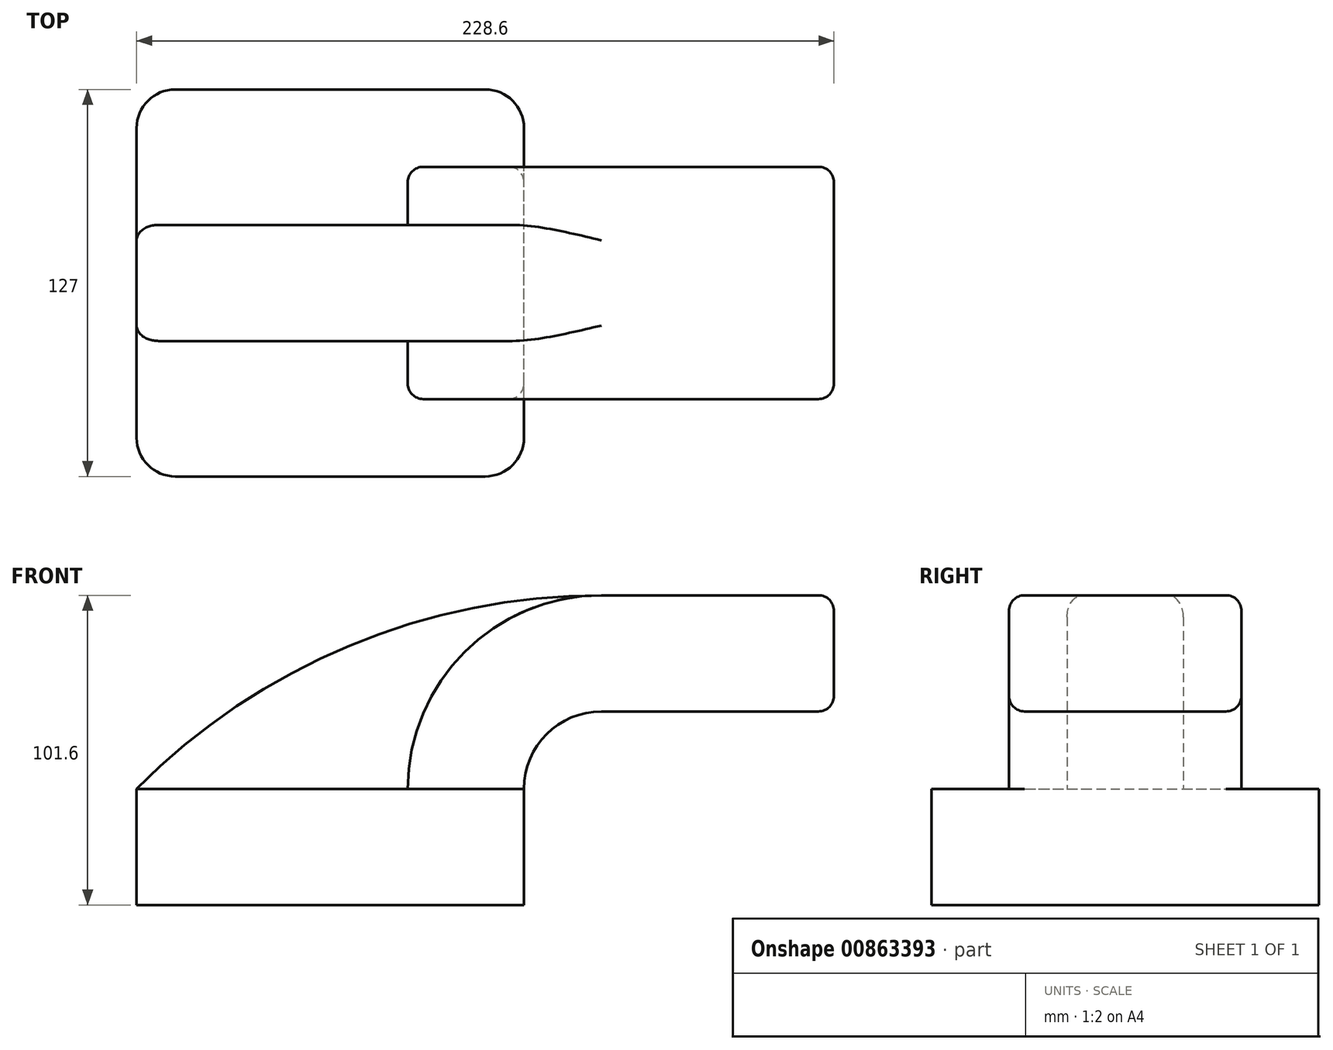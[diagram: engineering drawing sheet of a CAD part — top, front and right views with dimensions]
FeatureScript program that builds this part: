
annotation { "Feature Type Name" : "Feature", "Feature Type Description" : "" }
export const myFeature = defineFeature(function(context is Context, id is Id, definition is map)
    precondition{}
    {
        {
            var Q0;
            Q0=qCreatedBy(makeId("Front.planeOp"),FACE);
            var sketch = newSketch(context, id + "F0", { "sketchPlane" : qUnion([Q0])});
            skLineSegment(sketch, "E0.bottom", {"start": v(63.5, -19.05) * mm, "end": v(-63.5, -19.05) * mm});
            skLineSegment(sketch, "E0.top", {"start": v(63.5, 19.05) * mm, "end": v(-63.5, 19.05) * mm});
            skLineSegment(sketch, "E0.left", {"start": v(63.5, -19.05) * mm, "end": v(63.5, 19.05) * mm});
            skLineSegment(sketch, "E0.right", {"start": v(-63.5, -19.05) * mm, "end": v(-63.5, 19.05) * mm});
            skPoint(sketch, "E0.middle", {"position": v(0, 0) * mm});
            skPoint(sketch, "E1.middle", {"position": v(0, -116.97) * mm});
            skLineSegment(sketch, "E2.bottom", {"start": v(88.9, 44.45) * mm, "end": v(165.1, 44.45) * mm});
            skLineSegment(sketch, "E2.top", {"start": v(88.9, 82.55) * mm, "end": v(165.1, 82.55) * mm});
            skLineSegment(sketch, "E2.left", {"start": v(88.9, 44.45) * mm, "end": v(88.9, 82.55) * mm});
            skLineSegment(sketch, "E2.right", {"start": v(165.1, 44.45) * mm, "end": v(165.1, 82.55) * mm});
            skPoint(sketch, "E2.middle", {"position": v(127, 63.5) * mm});
            skArc(sketch, "E3", {"start": v(88.9, 44.45) * mm, "mid": v(70.94, 37.01) * mm, "end": v(63.5, 19.05) * mm});
            skArc(sketch, "E4.0", {"start": v(88.9, 82.55) * mm, "mid": v(44, 63.95) * mm, "end": v(25.4, 19.05) * mm});
            skArc(sketch, "E5", {"start": v(88.9, 82.55) * mm, "mid": v(6.35, 66.04) * mm, "end": v(-63.5, 19.05) * mm});
            skSolve(sketch);
        }
        {
            var Q0;
            Q0=makeQuery(id+"F0.imprint","IMPRINT",FACE,{"disambiguationData":[TD([[makeQuery(id+"F0.imprint","IMPRINT",EDGE,{"derivedFrom":sQuery(id+"F0.wireOp",EDGE,"E0.bottom")}),-1.0]])]});
            extrude(context, id + "F1", {"entities" : qUnion([Q0]), "endBound" : BoundingType.SYMMETRIC, "depth" : 127 * mm, "offsetDistance" : 25.4 * mm});
        }
        {
            var Q0;
            {var subQ2=sQuery(id+"F0.wireOp",EDGE,"E4.0");Q0=makeQuery(id+"F0.imprint","IMPRINT",FACE,{"disambiguationData":[TD([[makeQuery(id+"F0.imprint","IMPRINT",EDGE,{"derivedFrom":subQ2}),-1.0]])]});}
            extrude(context, id + "F2", {"entities" : qUnion([Q0]), "operationType" : NewBodyOperationType.ADD, "endBound" : BoundingType.SYMMETRIC, "depth" : 38.1 * mm, "offsetDistance" : 25.4 * mm});
        }
        {
            var Q0;
            Q0=makeQuery(id+"F0.imprint","IMPRINT",FACE,{"disambiguationData":[TD([[makeQuery(id+"F0.imprint","IMPRINT",EDGE,{"derivedFrom":sQuery(id+"F0.wireOp",EDGE,"E2.left")}),1.0]])]});
            extrude(context, id + "F3", {"entities" : qUnion([Q0]), "operationType" : NewBodyOperationType.ADD, "endBound" : BoundingType.SYMMETRIC, "depth" : 76.2 * mm, "offsetDistance" : 25.4 * mm});
        }
        {
            var Q0;
            Q0=makeQuery(id+"F0.imprint","IMPRINT",FACE,{"disambiguationData":[TD([[makeQuery(id+"F0.imprint","IMPRINT",EDGE,{"derivedFrom":sQuery(id+"F0.wireOp",EDGE,"E2.bottom")}),1.0]])]});
            extrude(context, id + "F4", {"entities" : qUnion([Q0]), "operationType" : NewBodyOperationType.ADD, "endBound" : BoundingType.SYMMETRIC, "depth" : 76.2 * mm, "offsetDistance" : 25.4 * mm});
        }
        {
            var Q0;
            Q0=makeQuery(id+"F1.opExtrude","CAP_EDGE",EDGE,{"disambiguationData":[OSD([sQuery(id+"F0.wireOp",EDGE,"E0.left")])],"isStart":false});
            var Q1;
            Q1=makeQuery(id+"F1.opExtrude","CAP_EDGE",EDGE,{"disambiguationData":[OSD([sQuery(id+"F0.wireOp",EDGE,"E0.left")])],"isStart":true});
            var Q2;
            Q2=makeQuery(id+"F1.opExtrude","CAP_EDGE",EDGE,{"disambiguationData":[OSD([sQuery(id+"F0.wireOp",EDGE,"E0.right")])],"isStart":true});
            var Q3;
            Q3=makeQuery(id+"F1.opExtrude","CAP_EDGE",EDGE,{"disambiguationData":[OSD([sQuery(id+"F0.wireOp",EDGE,"E0.right")])],"isStart":false});
            fillet(context, id + "F5", {"entities" : qUnion([Q0, Q1, Q2, Q3]), "radius" : 12.7 * mm, "tangentPropagation" : true, "allowEdgeOverflow" : false});
        }
        {
            var Q0;
            Q0=makeQuery(id+"F2.opExtrude","CAP_EDGE",EDGE,{"disambiguationData":[OSD([sQuery(id+"F0.wireOp",EDGE,"E5")])],"isStart":false});
            var Q1;
            Q1=makeQuery(id+"F2.opExtrude","CAP_EDGE",EDGE,{"disambiguationData":[OSD([sQuery(id+"F0.wireOp",EDGE,"E5")])],"isStart":true});
            var Q2;
            Q2=makeQuery(id+"F3.opExtrude","CAP_EDGE",EDGE,{"disambiguationData":[OSD([sQuery(id+"F0.wireOp",EDGE,"E4.0")])],"isStart":false});
            var Q3;
            Q3=makeQuery(id+"F4.opExtrude","CAP_EDGE",EDGE,{"disambiguationData":[OSD([sQuery(id+"F0.wireOp",EDGE,"E2.bottom")])],"isStart":false});
            var Q4;
            Q4=makeQuery(id+"F3.opExtrude","CAP_EDGE",EDGE,{"disambiguationData":[OSD([sQuery(id+"F0.wireOp",EDGE,"E3")])],"isStart":false});
            var Q5;
            Q5=makeQuery(id+"F3.opExtrude","CAP_EDGE",EDGE,{"disambiguationData":[OSD([sQuery(id+"F0.wireOp",EDGE,"E4.0")])],"isStart":true});
            var Q6;
            Q6=makeQuery(id+"F4.opExtrude","CAP_EDGE",EDGE,{"disambiguationData":[OSD([sQuery(id+"F0.wireOp",EDGE,"E2.bottom")])],"isStart":true});
            var Q7;
            Q7=makeQuery(id+"F4.opExtrude","SWEPT_EDGE",EDGE,{"disambiguationData":[OSD([sQuery(id+"F0.wireOp",EDGE,"E2.top"),sQuery(id+"F0.wireOp",EDGE,"E2.right")])]});
            var Q8;
            Q8=makeQuery(id+"F4.opExtrude","CAP_EDGE",EDGE,{"disambiguationData":[OSD([sQuery(id+"F0.wireOp",EDGE,"E2.right")])],"isStart":true});
            var Q9;
            Q9=makeQuery(id+"F4.opExtrude","SWEPT_EDGE",EDGE,{"disambiguationData":[OSD([sQuery(id+"F0.wireOp",EDGE,"E2.bottom"),sQuery(id+"F0.wireOp",EDGE,"E2.right")])]});
            var Q10;
            Q10=makeQuery(id+"F4.opExtrude","CAP_EDGE",EDGE,{"disambiguationData":[OSD([sQuery(id+"F0.wireOp",EDGE,"E2.right")])],"isStart":false});
            fillet(context, id + "F6", {"entities" : qUnion([Q0, Q1, Q2, Q3, Q4, Q5, Q6, Q7, Q8, Q9, Q10]), "radius" : 5.08 * mm, "tangentPropagation" : true, "allowEdgeOverflow" : false});
        }
    });
